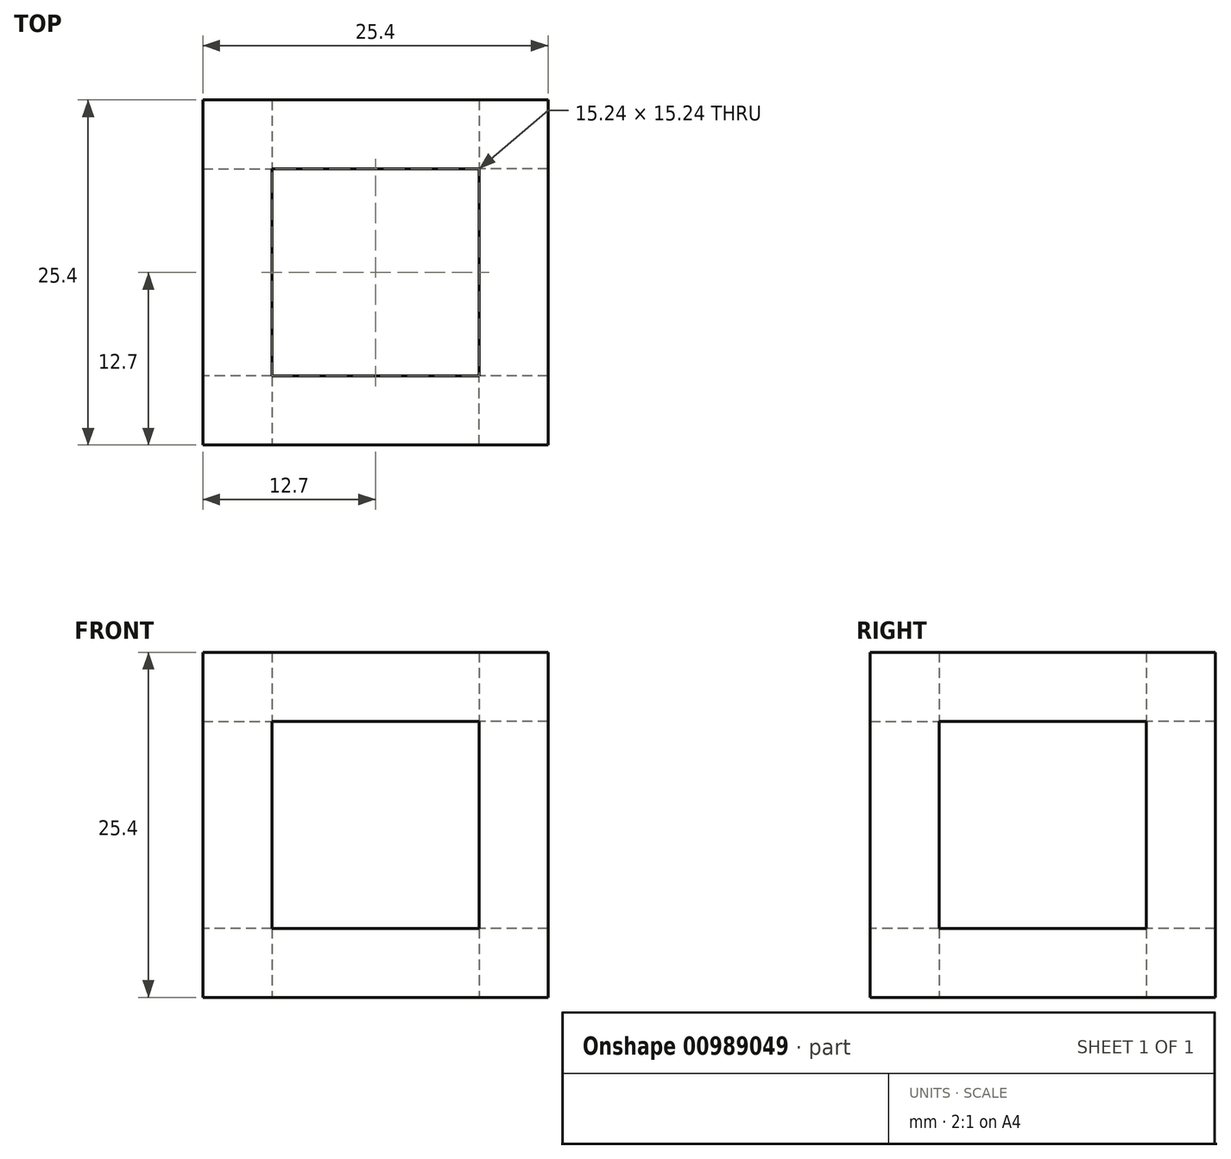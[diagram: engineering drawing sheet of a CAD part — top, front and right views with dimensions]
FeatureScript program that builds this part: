
annotation { "Feature Type Name" : "Feature", "Feature Type Description" : "" }
export const myFeature = defineFeature(function(context is Context, id is Id, definition is map)
    precondition{}
    {
        {
            var Q0;
            Q0=qCreatedBy(makeId("Top.planeOp"),FACE);
            var sketch = newSketch(context, id + "F0", { "sketchPlane" : qUnion([Q0])});
            skLineSegment(sketch, "E0.bottom", {"start": v(12.7, 12.7) * mm, "end": v(-12.7, 12.7) * mm});
            skLineSegment(sketch, "E0.top", {"start": v(12.7, -12.7) * mm, "end": v(-12.7, -12.7) * mm});
            skLineSegment(sketch, "E0.left", {"start": v(12.7, 12.7) * mm, "end": v(12.7, -12.7) * mm});
            skLineSegment(sketch, "E0.right", {"start": v(-12.7, 12.7) * mm, "end": v(-12.7, -12.7) * mm});
            skPoint(sketch, "E0.middle", {"position": v(0, 0) * mm});
            skLineSegment(sketch, "E1.0", {"start": v(-7.62, 7.62) * mm, "end": v(-7.62, -7.62) * mm});
            skLineSegment(sketch, "E1.1", {"start": v(7.62, 7.62) * mm, "end": v(-7.62, 7.62) * mm});
            skLineSegment(sketch, "E1.2", {"start": v(7.62, 7.62) * mm, "end": v(7.62, -7.62) * mm});
            skLineSegment(sketch, "E1.3", {"start": v(7.62, -7.62) * mm, "end": v(-7.62, -7.62) * mm});
            skSolve(sketch);
        }
        {
            var Q0;
            Q0 = qSketchRegion(id + "F0", true);
            extrude(context, id + "F1", {"entities" : qUnion([Q0]), "depth" : 5.08 * mm, "offsetDistance" : 25.4 * mm});
        }
        {
            var Q0;
            Q0=makeQuery(id+"F1.opExtrude","CAP_FACE",FACE,{"disambiguationData":[OSD([sQuery(id+"F0.wireOp",EDGE,"E0.bottom"),sQuery(id+"F0.wireOp",EDGE,"E0.top"),sQuery(id+"F0.wireOp",EDGE,"E0.left"),sQuery(id+"F0.wireOp",EDGE,"E0.right"),sQuery(id+"F0.wireOp",EDGE,"E1.0"),sQuery(id+"F0.wireOp",EDGE,"E1.1"),sQuery(id+"F0.wireOp",EDGE,"E1.2"),sQuery(id+"F0.wireOp",EDGE,"E1.3")])],"isStart":false});
            var sketch = newSketch(context, id + "F2", { "sketchPlane" : qUnion([Q0])});
            skLineSegment(sketch, "E2.bottom", {"start": v(-12.7, 12.7) * mm, "end": v(-7.62, 12.7) * mm});
            skLineSegment(sketch, "E2.top", {"start": v(-12.7, 7.62) * mm, "end": v(-7.62, 7.62) * mm});
            skLineSegment(sketch, "E2.left", {"start": v(-12.7, 12.7) * mm, "end": v(-12.7, 7.62) * mm});
            skLineSegment(sketch, "E2.right", {"start": v(-7.62, 12.7) * mm, "end": v(-7.62, 7.62) * mm});
            skLineSegment(sketch, "E3.bottom", {"start": v(12.7, 12.7) * mm, "end": v(7.62, 12.7) * mm});
            skLineSegment(sketch, "E3.top", {"start": v(12.7, 7.62) * mm, "end": v(7.62, 7.62) * mm});
            skLineSegment(sketch, "E3.left", {"start": v(12.7, 12.7) * mm, "end": v(12.7, 7.62) * mm});
            skLineSegment(sketch, "E3.right", {"start": v(7.62, 12.7) * mm, "end": v(7.62, 7.62) * mm});
            skLineSegment(sketch, "E4.bottom", {"start": v(12.7, -12.7) * mm, "end": v(7.62, -12.7) * mm});
            skLineSegment(sketch, "E4.top", {"start": v(12.7, -7.62) * mm, "end": v(7.62, -7.62) * mm});
            skLineSegment(sketch, "E4.left", {"start": v(12.7, -12.7) * mm, "end": v(12.7, -7.62) * mm});
            skLineSegment(sketch, "E4.right", {"start": v(7.62, -12.7) * mm, "end": v(7.62, -7.62) * mm});
            skLineSegment(sketch, "E5.bottom", {"start": v(-7.62, -7.62) * mm, "end": v(-12.7, -7.62) * mm});
            skLineSegment(sketch, "E5.top", {"start": v(-7.62, -12.7) * mm, "end": v(-12.7, -12.7) * mm});
            skLineSegment(sketch, "E5.left", {"start": v(-7.62, -7.62) * mm, "end": v(-7.62, -12.7) * mm});
            skLineSegment(sketch, "E5.right", {"start": v(-12.7, -7.62) * mm, "end": v(-12.7, -12.7) * mm});
            skSolve(sketch);
        }
        {
            var Q0;
            Q0 = qSketchRegion(id + "F2", true);
            extrude(context, id + "F3", {"entities" : qUnion([Q0]), "operationType" : NewBodyOperationType.ADD, "depth" : 15.24 * mm, "offsetDistance" : 25.4 * mm});
        }
        {
            var Q0;
            Q0=makeQuery(id+"F3.opExtrude","CAP_FACE",FACE,{"disambiguationData":[OSD([sQuery(id+"F2.wireOp",EDGE,"E2.bottom"),sQuery(id+"F2.wireOp",EDGE,"E2.top"),sQuery(id+"F2.wireOp",EDGE,"E2.left"),sQuery(id+"F2.wireOp",EDGE,"E2.right")])],"isStart":false});
            var sketch = newSketch(context, id + "F4", { "sketchPlane" : qUnion([Q0])});
            skLineSegment(sketch, "E6.bottom", {"start": v(-12.7, 12.7) * mm, "end": v(12.7, 12.7) * mm});
            skLineSegment(sketch, "E6.top", {"start": v(-12.7, -12.7) * mm, "end": v(12.7, -12.7) * mm});
            skLineSegment(sketch, "E6.left", {"start": v(-12.7, 12.7) * mm, "end": v(-12.7, -12.7) * mm});
            skLineSegment(sketch, "E6.right", {"start": v(12.7, 12.7) * mm, "end": v(12.7, -12.7) * mm});
            skLineSegment(sketch, "E7.0", {"start": v(-7.62, 7.62) * mm, "end": v(-7.62, -7.62) * mm});
            skLineSegment(sketch, "E7.1", {"start": v(-7.62, 7.62) * mm, "end": v(7.62, 7.62) * mm});
            skLineSegment(sketch, "E7.2", {"start": v(7.62, 7.62) * mm, "end": v(7.62, -7.62) * mm});
            skLineSegment(sketch, "E7.3", {"start": v(-7.62, -7.62) * mm, "end": v(7.62, -7.62) * mm});
            skSolve(sketch);
        }
        {
            var Q0;
            Q0 = qSketchRegion(id + "F4", true);
            extrude(context, id + "F5", {"entities" : qUnion([Q0]), "operationType" : NewBodyOperationType.ADD, "depth" : 5.08 * mm, "offsetDistance" : 25.4 * mm});
        }
    });
